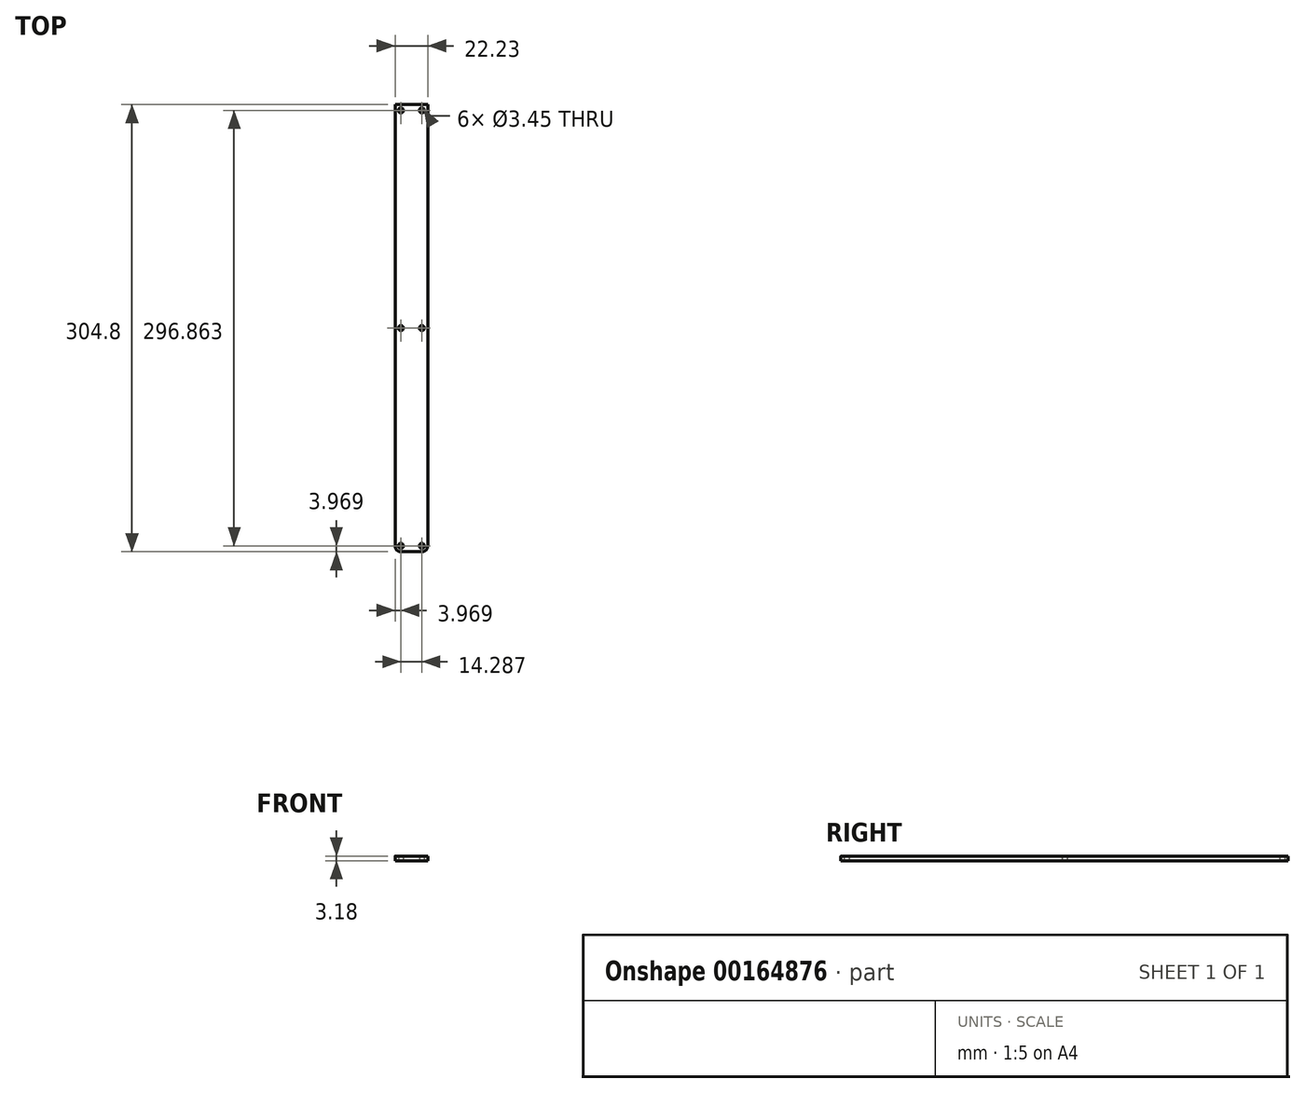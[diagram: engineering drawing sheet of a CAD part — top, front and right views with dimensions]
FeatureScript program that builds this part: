
annotation { "Feature Type Name" : "Feature", "Feature Type Description" : "" }
export const myFeature = defineFeature(function(context is Context, id is Id, definition is map)
    precondition{}
    {
        {
            var Q0;
            Q0=qCreatedBy(makeId("Top.planeOp"),FACE);
            var sketch = newSketch(context, id + "F0", { "sketchPlane" : qUnion([Q0])});
            skLineSegment(sketch, "E0.bottom", {"start": v(0, 0) * mm, "end": v(22.22, 0) * mm});
            skLineSegment(sketch, "E0.top", {"start": v(0, -304.8) * mm, "end": v(22.23, -304.8) * mm});
            skLineSegment(sketch, "E0.left", {"start": v(0, 0) * mm, "end": v(0, -304.8) * mm});
            skLineSegment(sketch, "E0.right", {"start": v(22.23, 0) * mm, "end": v(22.23, -304.8) * mm});
            skLineSegment(sketch, "E1", {"start": v(11.11, 0) * mm, "end": v(11.11, -304.8) * mm, "construction": true});
            skLineSegment(sketch, "E2", {"start": v(3.97, 0) * mm, "end": v(3.97, -3.97) * mm, "construction": true});
            skLineSegment(sketch, "E3", {"start": v(3.97, -3.97) * mm, "end": v(0, -3.97) * mm, "construction": true});
            skLineSegment(sketch, "E4.bottom", {"start": v(3.97, -3.97) * mm, "end": v(18.26, -3.97) * mm, "construction": true});
            skLineSegment(sketch, "E4.top", {"start": v(3.97, -300.83) * mm, "end": v(18.26, -300.83) * mm, "construction": true});
            skLineSegment(sketch, "E4.left", {"start": v(3.97, -3.97) * mm, "end": v(3.97, -300.83) * mm, "construction": true});
            skLineSegment(sketch, "E4.right", {"start": v(18.26, -3.97) * mm, "end": v(18.26, -300.83) * mm, "construction": true});
            skPoint(sketch, "E4.middle", {"position": v(11.11, -152.4) * mm});
            skCircle(sketch, "E5", {"center": v(3.97, -3.97) * mm, "radius": 1.73 * mm});
            skCircle(sketch, "E6", {"center": v(18.26, -3.97) * mm, "radius": 1.73 * mm});
            skCircle(sketch, "E7", {"center": v(18.26, -300.83) * mm, "radius": 1.73 * mm});
            skCircle(sketch, "E8", {"center": v(3.97, -300.83) * mm, "radius": 1.73 * mm});
            skCircle(sketch, "E9", {"center": v(18.26, -152.4) * mm, "radius": 1.73 * mm});
            skCircle(sketch, "E10", {"center": v(3.97, -152.4) * mm, "radius": 1.73 * mm});
            skSolve(sketch);
        }
        {
            var Q0;
            Q0 = qSketchRegion(id + "F0", true);
            extrude(context, id + "F1", {"entities" : qUnion([Q0]), "depth" : 3.17 * mm});
        }
        {
            var Q0;
            Q0=makeQuery(id+"F1.opExtrude","SWEPT_EDGE",EDGE,{"disambiguationData":[OSD([sQuery(id+"F0.wireOp",EDGE,"E0.top"),sQuery(id+"F0.wireOp",EDGE,"E0.left")])]});
            var Q1;
            Q1=makeQuery(id+"F1.opExtrude","SWEPT_EDGE",EDGE,{"disambiguationData":[OSD([sQuery(id+"F0.wireOp",EDGE,"E0.top"),sQuery(id+"F0.wireOp",EDGE,"E0.right")])]});
            fillet(context, id + "F2", {"entities" : qUnion([Q0, Q1]), "radius" : 3.97 * mm, "tangentPropagation" : true, "allowEdgeOverflow" : false});
        }
    });
